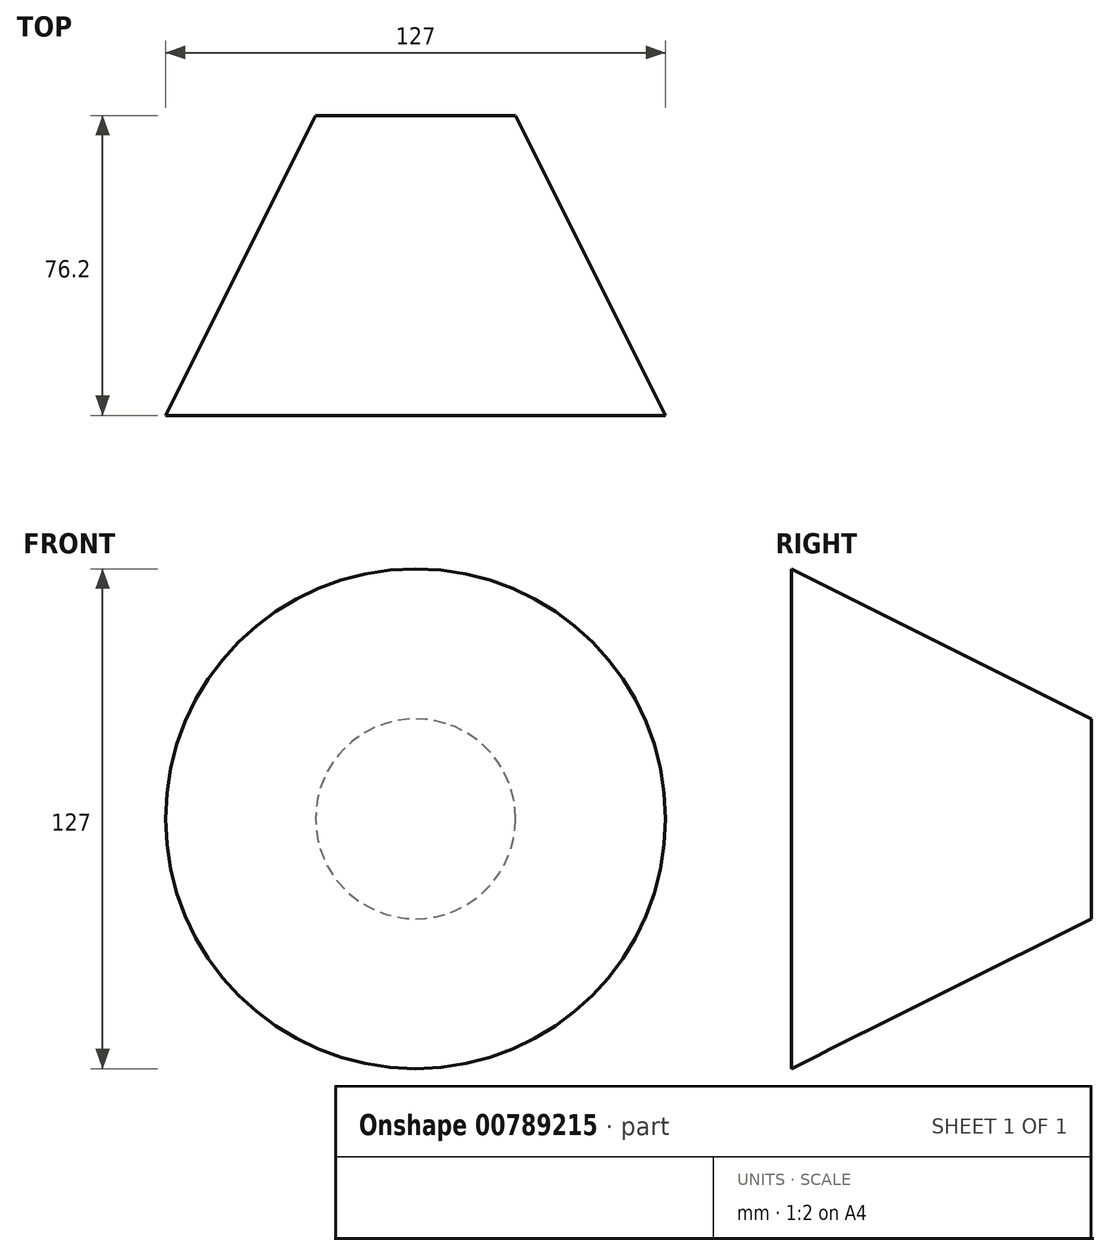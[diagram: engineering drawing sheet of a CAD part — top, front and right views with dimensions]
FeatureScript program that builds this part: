
annotation { "Feature Type Name" : "Feature", "Feature Type Description" : "" }
export const myFeature = defineFeature(function(context is Context, id is Id, definition is map)
    precondition{}
    {
        {
            var Q0;
            Q0=qCreatedBy(makeId("Front.planeOp"),FACE);
            var sketch = newSketch(context, id + "F0", { "sketchPlane" : qUnion([Q0])});
            skCircle(sketch, "E0", {"center": v(0, 0) * mm, "radius": 63.5 * mm});
            skSolve(sketch);
        }
        {
            var Q0;
            Q0=qCreatedBy(makeId("Front.planeOp"),FACE);
            cPlane(context, id + "F1", {"entities" : qUnion([Q0]), "cplaneType" : CPlaneType.OFFSET, "offset" : 76.2 * mm, "oppositeDirection" : true, "width" : 152.4 * mm, "height" : 152.4 * mm});
        }
        {
            var Q0;
            Q0=qCreatedBy(id+"F1.planeOp",FACE);
            var sketch = newSketch(context, id + "F2", { "sketchPlane" : qUnion([Q0])});
            skCircle(sketch, "E1", {"center": v(0, 0) * mm, "radius": 25.4 * mm});
            skSolve(sketch);
        }
        {
            var Q0;
            Q0=makeQuery(id+"F0.imprint","IMPRINT",FACE,{"disambiguationData":[TD([[makeQuery(id+"F0.imprint","IMPRINT",EDGE,{"derivedFrom":sQuery(id+"F0.wireOp",EDGE,"E0")}),1.0]])]});
            var Q1;
            Q1=makeQuery(id+"F2.imprint","IMPRINT",FACE,{"disambiguationData":[TD([[makeQuery(id+"F2.imprint","IMPRINT",EDGE,{"derivedFrom":sQuery(id+"F2.wireOp",EDGE,"E1")}),1.0]])]});
            loft(context, id + "F3", {"sheetProfilesArray" : [{ "sheetProfileEntities" : qUnion([Q0]) }, { "sheetProfileEntities" : qUnion([Q1]) }]});
        }
    });
